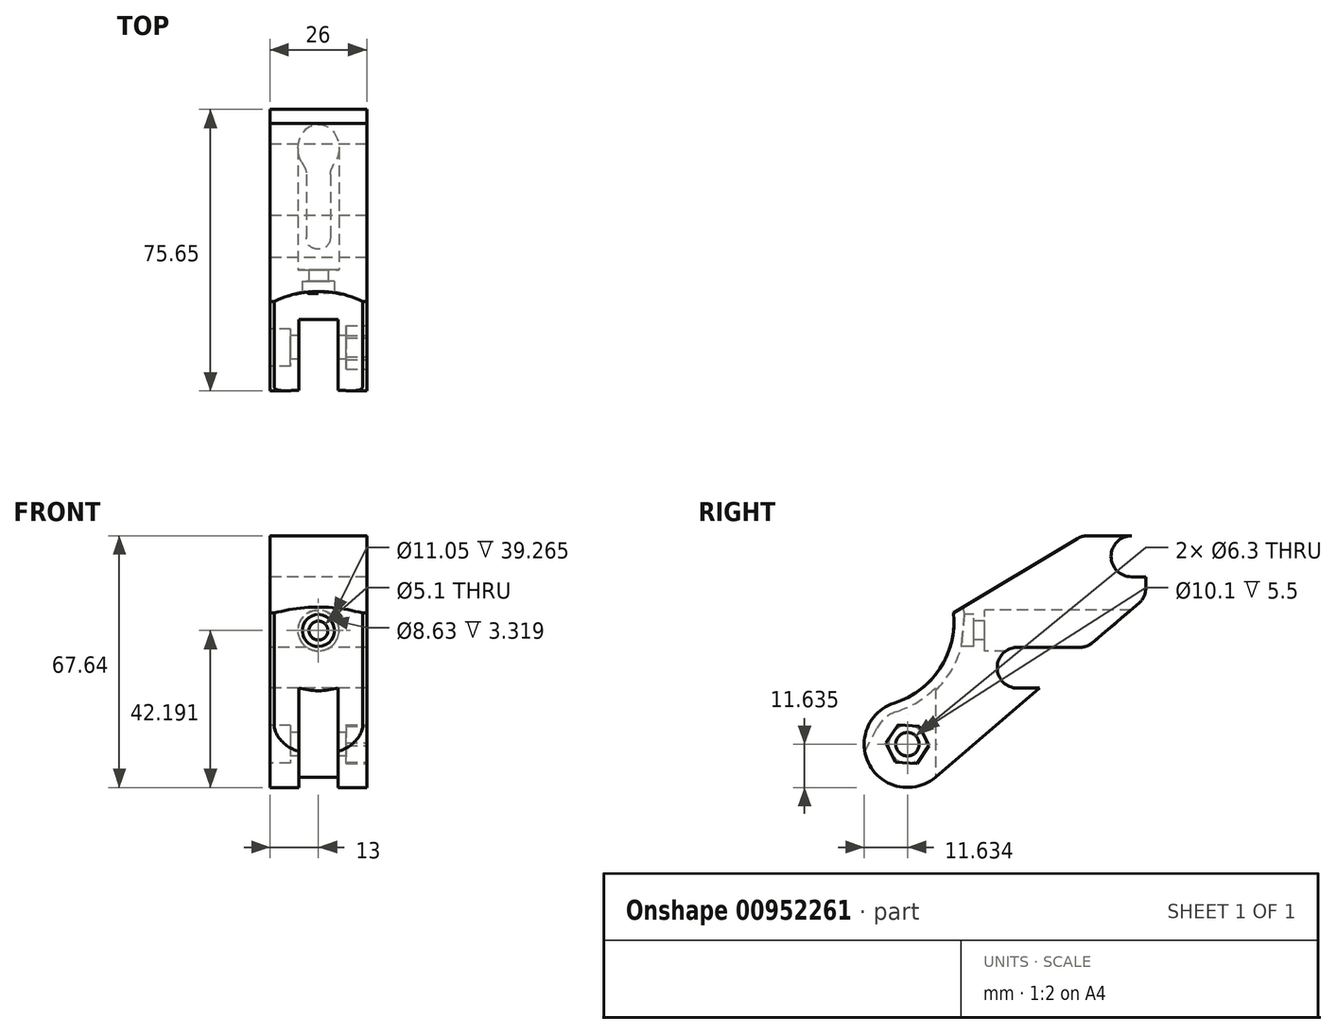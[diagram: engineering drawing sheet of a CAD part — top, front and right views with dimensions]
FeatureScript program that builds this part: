
annotation { "Feature Type Name" : "Feature", "Feature Type Description" : "" }
export const myFeature = defineFeature(function(context is Context, id is Id, definition is map)
    precondition{}
    {
        {
            var Q0;
            Q0=qCreatedBy(makeId("Right.planeOp"),FACE);
            var sketch = newSketch(context, id + "F0", { "sketchPlane" : qUnion([Q0])});
            skArc(sketch, "E0", {"start": v(0.2, 3.87) * mm, "mid": v(-5.3, -1.63) * mm, "end": v(0.2, -7.13) * mm});
            skLineSegment(sketch, "E1", {"start": v(-17.01, 13.06) * mm, "end": v(16.2, 33.1) * mm});
            skArc(sketch, "E2", {"start": v(-32.93, -11.1) * mm, "mid": v(-20.7, -1.84) * mm, "end": v(-17.01, 13.06) * mm});
            skLineSegment(sketch, "E3", {"start": v(30.79, 33.82) * mm, "end": v(18.78, 33.82) * mm});
            skLineSegment(sketch, "E4", {"start": v(30.79, 22.82) * mm, "end": v(34.61, 22.82) * mm});
            skLineSegment(sketch, "E5", {"start": v(0.2, -7.13) * mm, "end": v(6.06, -7.13) * mm});
            skLineSegment(sketch, "E6", {"start": v(0.2, 3.87) * mm, "end": v(17.06, 3.87) * mm});
            skArc(sketch, "E7", {"start": v(30.79, 33.82) * mm, "mid": v(25.29, 28.32) * mm, "end": v(30.79, 22.82) * mm});
            skLineSegment(sketch, "E8", {"start": v(6.06, -7.13) * mm, "end": v(-21.84, -31.02) * mm});
            skLineSegment(sketch, "E9", {"start": v(32.86, 15.82) * mm, "end": v(20.31, 5.07) * mm});
            skArc(sketch, "E10", {"start": v(-32.93, -11.1) * mm, "mid": v(-39.57, -27.84) * mm, "end": v(-21.84, -31.02) * mm});
            skCircle(sketch, "E11", {"center": v(-29.4, -22.18) * mm, "radius": 3.15 * mm});
            skLineSegment(sketch, "E12", {"start": v(34.61, 19.62) * mm, "end": v(34.61, 22.82) * mm});
            skPoint(sketch, "E13.visualSharp", {"position": v(34.61, 17.31) * mm});
            skArc(sketch, "E13.filletArc", {"start": v(32.86, 15.82) * mm, "mid": v(34.15, 17.52) * mm, "end": v(34.61, 19.62) * mm});
            skPoint(sketch, "E14.visualSharp", {"position": v(18.9, 3.87) * mm});
            skArc(sketch, "E14.filletArc", {"start": v(17.06, 3.87) * mm, "mid": v(18.8, 4.18) * mm, "end": v(20.31, 5.07) * mm});
            skPoint(sketch, "E15.visualSharp", {"position": v(17.4, 33.82) * mm});
            skArc(sketch, "E15.filletArc", {"start": v(18.78, 33.82) * mm, "mid": v(17.44, 33.63) * mm, "end": v(16.2, 33.1) * mm});
            skSolve(sketch);
        }
        {
            var Q0;
            Q0=makeQuery(id+"F0.imprint","IMPRINT",FACE,{"disambiguationData":[TD([[makeQuery(id+"F0.imprint","IMPRINT",EDGE,{"derivedFrom":sQuery(id+"F0.wireOp",EDGE,"E0")}),-1.0]])]});
            extrude(context, id + "F1", {"entities" : qUnion([Q0]), "endBound" : BoundingType.SYMMETRIC, "depth" : 26 * mm, "offsetDistance" : 25 * mm});
        }
        {
            var Q0;
            Q0=qCreatedBy(makeId("Right.planeOp"),FACE);
            var sketch = newSketch(context, id + "F2", { "sketchPlane" : qUnion([Q0])});
            skArc(sketch, "E16", {"start": v(-32.93, -11.1) * mm, "mid": v(-26.85, -8.12) * mm, "end": v(-21.9, -3.5) * mm});
            skArc(sketch, "E17", {"start": v(-32.93, -11.1) * mm, "mid": v(-39.57, -27.84) * mm, "end": v(-21.84, -31.02) * mm});
            skLineSegment(sketch, "E18", {"start": v(-21.9, -3.5) * mm, "end": v(-21.9, -31.07) * mm});
            skSolve(sketch);
        }
        {
            var Q0;
            Q0 = qSketchRegion(id + "F2", true);
            extrude(context, id + "F3", {"entities" : qUnion([Q0]), "operationType" : NewBodyOperationType.REMOVE, "endBound" : BoundingType.SYMMETRIC, "oppositeDirection" : true, "depth" : 10.5 * mm, "offsetDistance" : 25 * mm});
        }
        {
            var Q0;
            Q0=makeQuery(id+"F1.opExtrude","CAP_FACE",FACE,{"disambiguationData":[OSD([sQuery(id+"F0.wireOp",EDGE,"E0"),sQuery(id+"F0.wireOp",EDGE,"E1"),sQuery(id+"F0.wireOp",EDGE,"E2"),sQuery(id+"F0.wireOp",EDGE,"E3"),sQuery(id+"F0.wireOp",EDGE,"E4"),sQuery(id+"F0.wireOp",EDGE,"E5"),sQuery(id+"F0.wireOp",EDGE,"E6"),sQuery(id+"F0.wireOp",EDGE,"E7"),sQuery(id+"F0.wireOp",EDGE,"E8"),sQuery(id+"F0.wireOp",EDGE,"E9"),sQuery(id+"F0.wireOp",EDGE,"E10"),sQuery(id+"F0.wireOp",EDGE,"E11"),sQuery(id+"F0.wireOp",EDGE,"E12"),sQuery(id+"F0.wireOp",EDGE,"E13.filletArc"),sQuery(id+"F0.wireOp",EDGE,"E14.filletArc")])],"isStart":false});
            var sketch = newSketch(context, id + "F4", { "sketchPlane" : qUnion([Q0])});
            skCircle(sketch, "E19.cCircle", {"center": v(-29.4, -22.18) * mm, "radius": 5.05 * mm, "construction": true});
            skLineSegment(sketch, "E19.0", {"start": v(-23.59, -22.6) * mm, "end": v(-26.86, -27.43) * mm});
            skLineSegment(sketch, "E19.1", {"start": v(-26.86, -27.43) * mm, "end": v(-32.67, -27.02) * mm});
            skLineSegment(sketch, "E19.2", {"start": v(-32.67, -27.02) * mm, "end": v(-35.22, -21.77) * mm});
            skLineSegment(sketch, "E19.3", {"start": v(-35.22, -21.77) * mm, "end": v(-31.96, -16.94) * mm});
            skLineSegment(sketch, "E19.4", {"start": v(-31.96, -16.94) * mm, "end": v(-26.14, -17.35) * mm});
            skLineSegment(sketch, "E19.5", {"start": v(-26.14, -17.35) * mm, "end": v(-23.59, -22.6) * mm});
            skPoint(sketch, "E19.0.midPoint", {"position": v(-25.22, -25.01) * mm});
            skSolve(sketch);
        }
        {
            var Q0;
            Q0 = qSketchRegion(id + "F4", true);
            extrude(context, id + "F5", {"entities" : qUnion([Q0]), "operationType" : NewBodyOperationType.REMOVE, "oppositeDirection" : true, "depth" : 5.5 * mm, "offsetDistance" : 25 * mm});
        }
        {
            var Q0;
            Q0=makeQuery(id+"F1.opExtrude","CAP_FACE",FACE,{"disambiguationData":[OSD([sQuery(id+"F0.wireOp",EDGE,"E0"),sQuery(id+"F0.wireOp",EDGE,"E1"),sQuery(id+"F0.wireOp",EDGE,"E2"),sQuery(id+"F0.wireOp",EDGE,"E3"),sQuery(id+"F0.wireOp",EDGE,"E4"),sQuery(id+"F0.wireOp",EDGE,"E5"),sQuery(id+"F0.wireOp",EDGE,"E6"),sQuery(id+"F0.wireOp",EDGE,"E7"),sQuery(id+"F0.wireOp",EDGE,"E8"),sQuery(id+"F0.wireOp",EDGE,"E9"),sQuery(id+"F0.wireOp",EDGE,"E10"),sQuery(id+"F0.wireOp",EDGE,"E11"),sQuery(id+"F0.wireOp",EDGE,"E12"),sQuery(id+"F0.wireOp",EDGE,"E13.filletArc"),sQuery(id+"F0.wireOp",EDGE,"E14.filletArc")])],"isStart":true});
            var sketch = newSketch(context, id + "F6", { "sketchPlane" : qUnion([Q0])});
            skCircle(sketch, "E20", {"center": v(29.4, -22.18) * mm, "radius": 5.05 * mm});
            skSolve(sketch);
        }
        {
            var Q0;
            Q0 = qSketchRegion(id + "F6", true);
            extrude(context, id + "F7", {"entities" : qUnion([Q0]), "operationType" : NewBodyOperationType.REMOVE, "oppositeDirection" : true, "depth" : 5.5 * mm, "offsetDistance" : 25 * mm});
        }
        {
            var Q0;
            Q0=qCreatedBy(makeId("Right.planeOp"),FACE);
            var sketch = newSketch(context, id + "F8", { "sketchPlane" : qUnion([Q0])});
            skLineSegment(sketch, "E21", {"start": v(-8.6, 13.9) * mm, "end": v(31, 13.9) * mm});
            skLineSegment(sketch, "E22", {"start": v(31, 8.37) * mm, "end": v(-20.38, 8.37) * mm});
            skLineSegment(sketch, "E23", {"start": v(-8.6, 10.92) * mm, "end": v(-11.6, 10.92) * mm});
            skLineSegment(sketch, "E24", {"start": v(-11.6, 12.69) * mm, "end": v(-20.29, 12.69) * mm});
            skLineSegment(sketch, "E25", {"start": v(-11.6, 12.69) * mm, "end": v(-11.6, 10.92) * mm});
            skLineSegment(sketch, "E26", {"start": v(-8.6, 13.9) * mm, "end": v(-8.6, 10.92) * mm});
            skLineSegment(sketch, "E27", {"start": v(31, 13.9) * mm, "end": v(31, 8.37) * mm});
            skLineSegment(sketch, "E28", {"start": v(-20.38, 8.37) * mm, "end": v(-20.29, 12.69) * mm});
            skSolve(sketch);
        }
        {
            var Q0;
            Q0 = qSketchRegion(id + "F8", true);
            var Q1;
            Q1=sQuery(id+"F8.wireOp",EDGE,"E22");
            revolve(context, id + "F9", {"operationType" : NewBodyOperationType.REMOVE, "surfaceOperationType" : NewSurfaceOperationType.NEW, "entities" : qUnion([Q0]), "axis" : qUnion([Q1]), "revolveType" : RevolveType.FULL, "oppositeDirection" : true});
        }
        {
            var Q0;
            Q0=sQuery(id+"F0.wireOp",VERTEX,"E2.center");
            var Q1;
            Q1=sQuery(id+"F0.wireOp",VERTEX,"E10.center");
            var Q2;
            Q2=sQuery(id+"F4.wireOp",VERTEX,"E19.cCircle.center");
            cPlane(context, id + "F10", {"entities" : qUnion([Q0, Q1, Q2]), "cplaneType" : CPlaneType.THREE_POINT, "offset" : 25 * mm, "width" : 150 * mm, "height" : 150 * mm});
        }
        {
            var Q0;
            Q0=qCreatedBy(id+"F10.planeOp",FACE);
            var sketch = newSketch(context, id + "F11", { "sketchPlane" : qUnion([Q0])});
            skArc(sketch, "E29", {"start": v(-13, 0) * mm, "mid": v(0, -3.5) * mm, "end": v(13, 0) * mm});
            skLineSegment(sketch, "E30", {"start": v(13, 0) * mm, "end": v(-13, 0) * mm});
            skLineSegment(sketch, "E31", {"start": v(0, 22.34) * mm, "end": v(-13.52, 22.34) * mm, "construction": true});
            skLineSegment(sketch, "E32", {"start": v(0, -12.22) * mm, "end": v(-13, -12.22) * mm, "construction": true});
            skSolve(sketch);
        }
        {
            var Q0;
            Q0=makeQuery(id+"F11.imprint","IMPRINT",FACE,{"disambiguationData":[TD([[makeQuery(id+"F11.imprint","IMPRINT",EDGE,{"derivedFrom":sQuery(id+"F11.wireOp",EDGE,"E29")}),1.0]])]});
            var Q1;
            Q1=sQuery(id+"F11.wireOp",EDGE,"E31");
            revolve(context, id + "F12", {"operationType" : NewBodyOperationType.REMOVE, "surfaceOperationType" : NewSurfaceOperationType.NEW, "entities" : qUnion([Q0]), "axis" : qUnion([Q1]), "revolveType" : RevolveType.FULL, "oppositeDirection" : true});
        }
        {
            var Q0;
            Q0=makeQuery(id+"F11.imprint","IMPRINT",FACE,{"disambiguationData":[TD([[makeQuery(id+"F11.imprint","IMPRINT",EDGE,{"derivedFrom":sQuery(id+"F11.wireOp",EDGE,"E29")}),1.0]])]});
            var Q1;
            Q1=sQuery(id+"F11.wireOp",EDGE,"E32");
            revolve(context, id + "F13", {"operationType" : NewBodyOperationType.REMOVE, "surfaceOperationType" : NewSurfaceOperationType.NEW, "entities" : qUnion([Q0]), "axis" : qUnion([Q1]), "revolveType" : RevolveType.ONE_DIRECTION, "angle" : 45 * degree});
        }
        {
            var Q0;
            {var subQ0=sQuery(id+"F11.wireOp",EDGE,"E29");Q0=makeQuery(id+"F13.boolean.opBoolean","COPY",FACE,{"disambiguationData":[TD([makeQuery(id+"F3.boolean.opBoolean","COPY",FACE,{"derivedFrom":makeQuery(id+"F3.opExtrude","CAP_FACE",FACE,{"disambiguationData":[OSD([sQuery(id+"F2.wireOp",EDGE,"E16"),sQuery(id+"F2.wireOp",EDGE,"E17"),sQuery(id+"F2.wireOp",EDGE,"E18")])],"isStart":false})})])],"derivedFrom":makeQuery(id+"F13.opRevolve","CAP_FACE",FACE,{"disambiguationData":[OSD([subQ0,sQuery(id+"F11.wireOp",EDGE,"E30")])],"isStart":false})});}
            var Q1;
            {var subQ0=sQuery(id+"F11.wireOp",EDGE,"E29");Q1=makeQuery(id+"F13.boolean.opBoolean","COPY",FACE,{"disambiguationData":[TD([makeQuery(id+"F3.boolean.opBoolean","COPY",FACE,{"derivedFrom":makeQuery(id+"F3.opExtrude","CAP_FACE",FACE,{"disambiguationData":[OSD([sQuery(id+"F2.wireOp",EDGE,"E16"),sQuery(id+"F2.wireOp",EDGE,"E17"),sQuery(id+"F2.wireOp",EDGE,"E18")])],"isStart":true})})])],"derivedFrom":makeQuery(id+"F13.opRevolve","CAP_FACE",FACE,{"disambiguationData":[OSD([subQ0,sQuery(id+"F11.wireOp",EDGE,"E30")])],"isStart":false})});}
            extrude(context, id + "F14", {"entities" : qUnion([Q0, Q1]), "operationType" : NewBodyOperationType.REMOVE, "endBound" : BoundingType.THROUGH_ALL, "oppositeDirection" : true, "depth" : 25 * mm, "offsetDistance" : 25 * mm});
        }
    });
